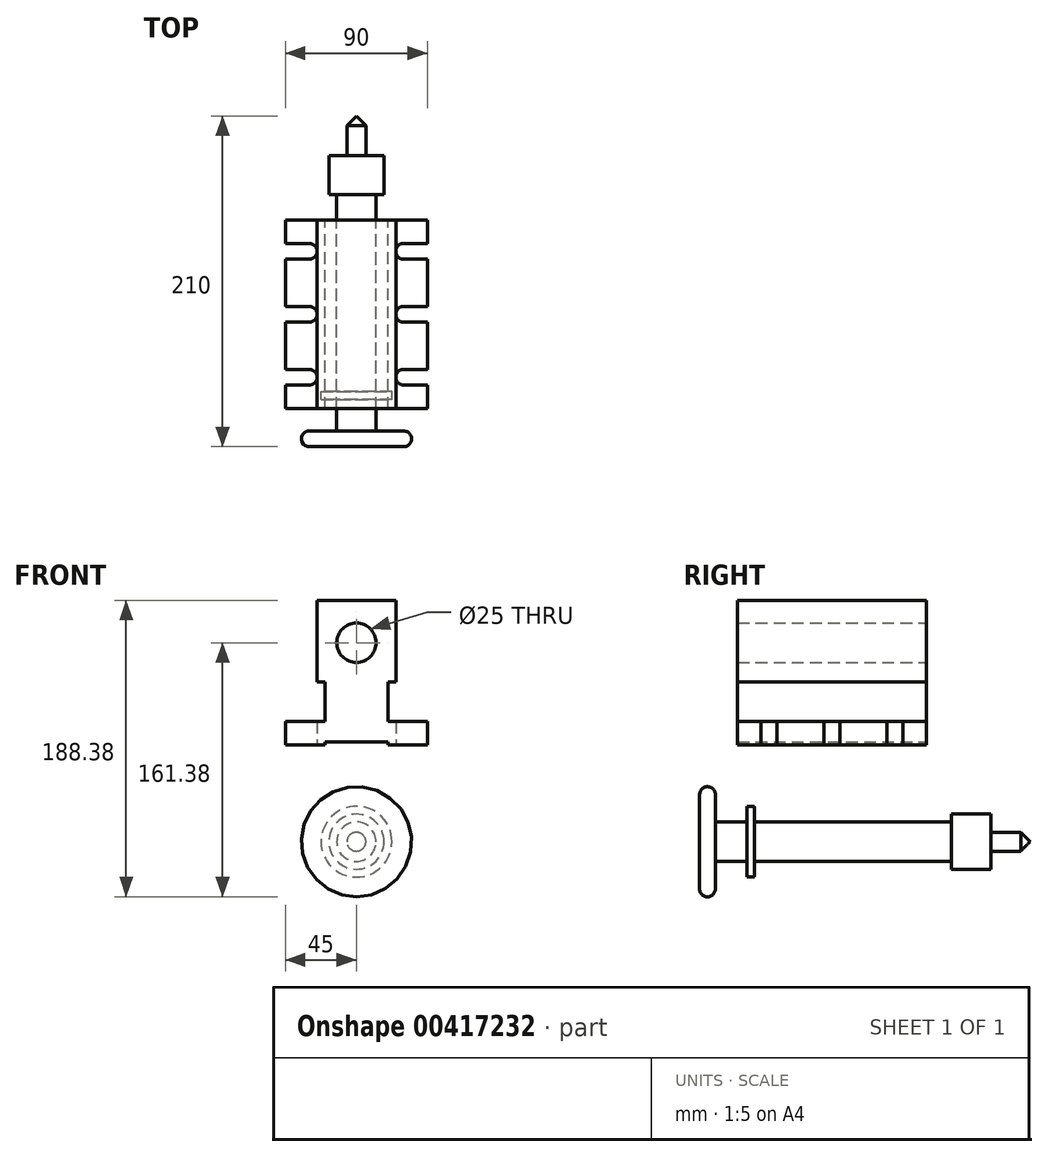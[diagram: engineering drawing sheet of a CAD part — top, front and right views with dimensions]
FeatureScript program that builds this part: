
annotation { "Feature Type Name" : "Feature", "Feature Type Description" : "" }
export const myFeature = defineFeature(function(context is Context, id is Id, definition is map)
    precondition{}
    {
        {
            var Q0;
            Q0=qCreatedBy(makeId("Front.planeOp"),FACE);
            var sketch = newSketch(context, id + "F0", { "sketchPlane" : qUnion([Q0])});
            skLineSegment(sketch, "E0", {"start": v(0, 2) * mm, "end": v(-20, 2) * mm});
            skLineSegment(sketch, "E1", {"start": v(-20, 2) * mm, "end": v(-20, 0) * mm});
            skLineSegment(sketch, "E2", {"start": v(-20, 0) * mm, "end": v(-45, 0) * mm});
            skLineSegment(sketch, "E3", {"start": v(-45, 0) * mm, "end": v(-45, 15) * mm});
            skLineSegment(sketch, "E4", {"start": v(-45, 15) * mm, "end": v(-20, 15) * mm});
            skLineSegment(sketch, "E5", {"start": v(-20, 15) * mm, "end": v(-20, 40) * mm});
            skLineSegment(sketch, "E6", {"start": v(-20, 40) * mm, "end": v(-25, 40) * mm});
            skLineSegment(sketch, "E7", {"start": v(-25, 40) * mm, "end": v(-25, 92) * mm});
            skLineSegment(sketch, "E8", {"start": v(-25, 92) * mm, "end": v(25, 92) * mm});
            skLineSegment(sketch, "E9", {"start": v(25, 92) * mm, "end": v(25, 40) * mm});
            skLineSegment(sketch, "E10", {"start": v(25, 40) * mm, "end": v(20, 40) * mm});
            skLineSegment(sketch, "E11", {"start": v(20, 40) * mm, "end": v(20, 15) * mm});
            skLineSegment(sketch, "E12", {"start": v(20, 15) * mm, "end": v(45, 15) * mm});
            skLineSegment(sketch, "E13", {"start": v(45, 15) * mm, "end": v(45, 0) * mm});
            skLineSegment(sketch, "E14", {"start": v(45, 0) * mm, "end": v(20, 0) * mm});
            skLineSegment(sketch, "E15", {"start": v(20, 0) * mm, "end": v(20, 2) * mm});
            skLineSegment(sketch, "E16", {"start": v(20, 2) * mm, "end": v(0, 2) * mm});
            skCircle(sketch, "E17", {"center": v(0, 65) * mm, "radius": 12.5 * mm});
            skSolve(sketch);
        }
        {
            var Q0;
            Q0=makeQuery(id+"F0.imprint","IMPRINT",FACE,{"disambiguationData":[TD([[makeQuery(id+"F0.imprint","IMPRINT",EDGE,{"derivedFrom":sQuery(id+"F0.wireOp",EDGE,"E0")}),-1.0]])]});
            extrude(context, id + "F1", {"entities" : qUnion([Q0]), "endBound" : BoundingType.SYMMETRIC, "depth" : 120 * mm});
        }
        {
            var Q0;
            Q0=makeQuery(id+"F1.opExtrude","SWEPT_FACE",FACE,{"disambiguationData":[OSD([sQuery(id+"F0.wireOp",EDGE,"E2")])]});
            var sketch = newSketch(context, id + "F2", { "sketchPlane" : qUnion([Q0])});
            skLineSegment(sketch, "E18", {"start": v(-30, 0) * mm, "end": v(-50, 0) * mm});
            skLineSegment(sketch, "E19", {"start": v(-30, 40) * mm, "end": v(-50, 40) * mm});
            skLineSegment(sketch, "E20", {"start": v(-30, -40) * mm, "end": v(-50, -40) * mm});
            skArc(sketch, "E21.0.startCap", {"start": v(-30, 45) * mm, "mid": v(-25, 40) * mm, "end": v(-30, 35) * mm});
            skArc(sketch, "E21.0.endCap", {"start": v(-50, 35) * mm, "mid": v(-55, 40) * mm, "end": v(-50, 45) * mm});
            skLineSegment(sketch, "E21.0.left", {"start": v(-30, 35) * mm, "end": v(-50, 35) * mm});
            skLineSegment(sketch, "E21.0.right", {"start": v(-30, 45) * mm, "end": v(-50, 45) * mm});
            skArc(sketch, "E22.0.startCap", {"start": v(-30, 5) * mm, "mid": v(-25, 0) * mm, "end": v(-30, -5) * mm});
            skArc(sketch, "E22.0.endCap", {"start": v(-50, -5) * mm, "mid": v(-55, 0) * mm, "end": v(-50, 5) * mm});
            skLineSegment(sketch, "E22.0.left", {"start": v(-30, -5) * mm, "end": v(-50, -5) * mm});
            skLineSegment(sketch, "E22.0.right", {"start": v(-30, 5) * mm, "end": v(-50, 5) * mm});
            skArc(sketch, "E23.0.startCap", {"start": v(-30, -35) * mm, "mid": v(-25, -40) * mm, "end": v(-30, -45) * mm});
            skArc(sketch, "E23.0.endCap", {"start": v(-50, -45) * mm, "mid": v(-55, -40) * mm, "end": v(-50, -35) * mm});
            skLineSegment(sketch, "E23.0.left", {"start": v(-30, -45) * mm, "end": v(-50, -45) * mm});
            skLineSegment(sketch, "E23.0.right", {"start": v(-30, -35) * mm, "end": v(-50, -35) * mm});
            skLineSegment(sketch, "E24.MirrorCS", {"start": v(30, 45) * mm, "end": v(50, 45) * mm});
            skLineSegment(sketch, "E25.MirrorCS", {"start": v(30, 35) * mm, "end": v(50, 35) * mm});
            skArc(sketch, "E26.MirrorCS", {"start": v(50, 35) * mm, "mid": v(55, 40) * mm, "end": v(50, 45) * mm});
            skArc(sketch, "E27.MirrorCS", {"start": v(30, 45) * mm, "mid": v(25, 40) * mm, "end": v(30, 35) * mm});
            skLineSegment(sketch, "E28.MirrorCS", {"start": v(30, -40) * mm, "end": v(50, -40) * mm});
            skLineSegment(sketch, "E29.MirrorCS", {"start": v(30, 40) * mm, "end": v(50, 40) * mm});
            skLineSegment(sketch, "E30.MirrorCS", {"start": v(30, 0) * mm, "end": v(50, 0) * mm});
            skArc(sketch, "E31.MirrorCS", {"start": v(30, 5) * mm, "mid": v(25, 0) * mm, "end": v(30, -5) * mm});
            skArc(sketch, "E32.MirrorCS", {"start": v(50, -5) * mm, "mid": v(55, 0) * mm, "end": v(50, 5) * mm});
            skLineSegment(sketch, "E33.MirrorCS", {"start": v(30, -5) * mm, "end": v(50, -5) * mm});
            skLineSegment(sketch, "E34.MirrorCS", {"start": v(30, 5) * mm, "end": v(50, 5) * mm});
            skArc(sketch, "E35.MirrorCS", {"start": v(30, -35) * mm, "mid": v(25, -40) * mm, "end": v(30, -45) * mm});
            skArc(sketch, "E36.MirrorCS", {"start": v(50, -45) * mm, "mid": v(55, -40) * mm, "end": v(50, -35) * mm});
            skLineSegment(sketch, "E37.MirrorCS", {"start": v(30, -35) * mm, "end": v(50, -35) * mm});
            skLineSegment(sketch, "E38.MirrorCS", {"start": v(30, -45) * mm, "end": v(50, -45) * mm});
            skSolve(sketch);
        }
        {
            var Q0;
            Q0 = qSketchRegion(id + "F2", true);
            extrude(context, id + "F3", {"entities" : qUnion([Q0]), "operationType" : NewBodyOperationType.REMOVE, "oppositeDirection" : true, "depth" : 25 * mm});
        }
        {
            var Q0;
            Q0=qCreatedBy(makeId("Right.planeOp"),FACE);
            var sketch = newSketch(context, id + "F4", { "sketchPlane" : qUnion([Q0])});
            skLineSegment(sketch, "E39", {"start": v(125.88, -61.38) * mm, "end": v(-84.12, -61.38) * mm});
            skLineSegment(sketch, "E40", {"start": v(-84.12, -61.38) * mm, "end": v(-84.12, -26.38) * mm});
            skLineSegment(sketch, "E41", {"start": v(-84.12, -26.38) * mm, "end": v(-74.12, -26.38) * mm});
            skLineSegment(sketch, "E42", {"start": v(-74.12, -26.38) * mm, "end": v(-74.12, -48.88) * mm});
            skLineSegment(sketch, "E43", {"start": v(-74.12, -48.88) * mm, "end": v(-54.12, -48.88) * mm});
            skLineSegment(sketch, "E44", {"start": v(-54.12, -48.88) * mm, "end": v(-54.12, -38.88) * mm});
            skLineSegment(sketch, "E45", {"start": v(-54.12, -38.88) * mm, "end": v(-49.12, -38.88) * mm});
            skLineSegment(sketch, "E46", {"start": v(-49.12, -38.88) * mm, "end": v(-49.12, -48.88) * mm});
            skLineSegment(sketch, "E47", {"start": v(-49.12, -48.88) * mm, "end": v(75.88, -48.88) * mm});
            skLineSegment(sketch, "E48", {"start": v(75.88, -48.88) * mm, "end": v(75.88, -43.88) * mm});
            skLineSegment(sketch, "E49", {"start": v(75.88, -43.88) * mm, "end": v(100.88, -43.88) * mm});
            skLineSegment(sketch, "E50", {"start": v(100.88, -43.88) * mm, "end": v(100.88, -55.38) * mm});
            skLineSegment(sketch, "E51", {"start": v(100.88, -55.38) * mm, "end": v(119.88, -55.38) * mm});
            skLineSegment(sketch, "E52", {"start": v(119.88, -55.38) * mm, "end": v(125.88, -61.38) * mm});
            skSolve(sketch);
        }
        {
            var Q0;
            Q0=makeQuery(id+"F4.imprint","IMPRINT",FACE,{"disambiguationData":[TD([[makeQuery(id+"F4.imprint","IMPRINT",EDGE,{"derivedFrom":sQuery(id+"F4.wireOp",EDGE,"E39")}),-1.0]])]});
            var Q1;
            Q1=sQuery(id+"F4.wireOp",EDGE,"E39");
            revolve(context, id + "F5", {"entities" : qUnion([Q0]), "axis" : qUnion([Q1]), "revolveType" : RevolveType.FULL});
        }
        {
            var Q0;
            Q0=makeQuery(id+"F5.opRevolve","SWEPT_EDGE",EDGE,{"disambiguationData":[OSD([sQuery(id+"F4.wireOp",EDGE,"E41"),sQuery(id+"F4.wireOp",EDGE,"E42")])]});
            var Q1;
            Q1=makeQuery(id+"F5.opRevolve","SWEPT_EDGE",EDGE,{"disambiguationData":[OSD([sQuery(id+"F4.wireOp",EDGE,"E40"),sQuery(id+"F4.wireOp",EDGE,"E41")])]});
            fillet(context, id + "F6", {"entities" : qUnion([Q0, Q1]), "radius" : 5 * mm, "tangentPropagation" : true, "allowEdgeOverflow" : false});
        }
    });
